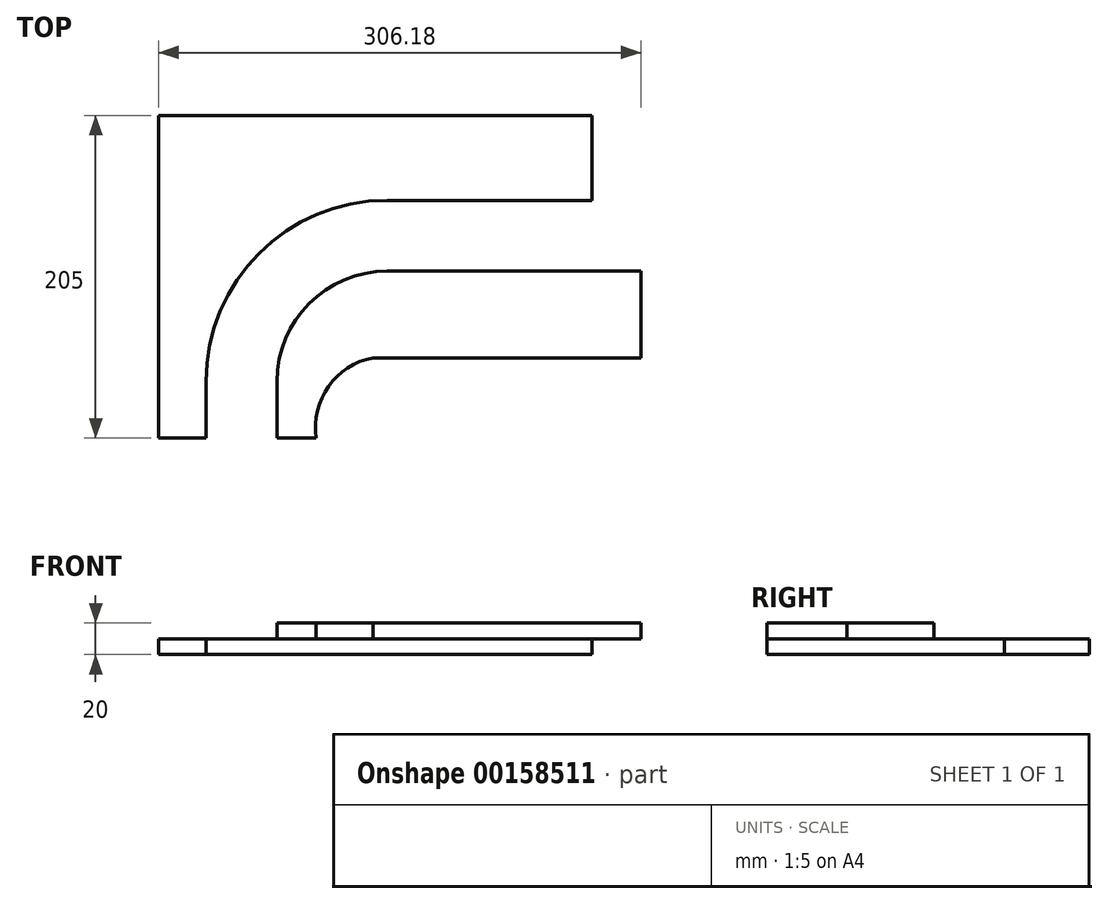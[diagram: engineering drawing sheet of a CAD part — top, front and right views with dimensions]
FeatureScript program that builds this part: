
annotation { "Feature Type Name" : "Feature", "Feature Type Description" : "" }
export const myFeature = defineFeature(function(context is Context, id is Id, definition is map)
    precondition{}
    {
        {
            var Q0;
            Q0=qCreatedBy(makeId("Top.planeOp"),FACE);
            var sketch = newSketch(context, id + "F0", { "sketchPlane" : qUnion([Q0])});
            skLineSegment(sketch, "E0.bottom", {"start": v(-230.67, 230.58) * mm, "end": v(44.33, 230.58) * mm});
            skLineSegment(sketch, "E0.top", {"start": v(-230.67, 25.58) * mm, "end": v(44.33, 25.58) * mm});
            skLineSegment(sketch, "E0.left", {"start": v(-230.67, 230.58) * mm, "end": v(-230.67, 25.58) * mm});
            skLineSegment(sketch, "E0.right", {"start": v(44.33, 230.58) * mm, "end": v(44.33, 25.58) * mm});
            skLineSegment(sketch, "E1.bottom", {"start": v(-209.28, -76.49) * mm, "end": v(30.72, -76.49) * mm});
            skLineSegment(sketch, "E1.top", {"start": v(-209.28, -196.49) * mm, "end": v(30.72, -196.49) * mm});
            skLineSegment(sketch, "E1.left", {"start": v(-209.28, -76.49) * mm, "end": v(-209.28, -196.49) * mm});
            skLineSegment(sketch, "E1.right", {"start": v(30.72, -76.49) * mm, "end": v(30.72, -196.49) * mm});
            skLineSegment(sketch, "E2", {"start": v(44.33, 230.58) * mm, "end": v(44.33, 176.58) * mm, "construction": true});
            skLineSegment(sketch, "E3", {"start": v(-230.67, 25.58) * mm, "end": v(-200.67, 25.58) * mm, "construction": true});
            skLineSegment(sketch, "E4", {"start": v(44.33, 176.58) * mm, "end": v(-85.67, 176.58) * mm, "construction": true});
            skLineSegment(sketch, "E5", {"start": v(-200.67, 25.58) * mm, "end": v(-200.67, 61.58) * mm, "construction": true});
            skLineSegment(sketch, "E6", {"start": v(-85.67, 176.58) * mm, "end": v(-85.67, 61.58) * mm, "construction": true});
            skLineSegment(sketch, "E7", {"start": v(-85.67, 61.58) * mm, "end": v(-200.67, 61.58) * mm, "construction": true});
            skCircle(sketch, "E8", {"center": v(-85.67, 61.58) * mm, "radius": 115 * mm});
            skLineSegment(sketch, "E9", {"start": v(-85.67, 176.58) * mm, "end": v(44.33, 176.58) * mm});
            skLineSegment(sketch, "E10", {"start": v(-200.67, 61.58) * mm, "end": v(-200.67, 25.58) * mm});
            skLineSegment(sketch, "E11", {"start": v(30.72, -76.49) * mm, "end": v(-94.48, -76.49) * mm, "construction": true});
            skLineSegment(sketch, "E12", {"start": v(-94.48, -76.49) * mm, "end": v(-94.48, -191.49) * mm, "construction": true});
            skCircle(sketch, "E13", {"center": v(-94.48, -191.49) * mm, "radius": 115 * mm});
            skLineSegment(sketch, "E14", {"start": v(30.72, -76.49) * mm, "end": v(30.72, -131.49) * mm, "construction": true});
            skLineSegment(sketch, "E15", {"start": v(30.72, -131.49) * mm, "end": v(-94.48, -131.49) * mm});
            skLineSegment(sketch, "E16", {"start": v(-209.28, -196.49) * mm, "end": v(-184.28, -196.49) * mm});
            skArc(sketch, "E17", {"start": v(-94.48, -131.49) * mm, "mid": v(-149.9, -149.44) * mm, "end": v(-184.28, -196.49) * mm});
            skLineSegment(sketch, "E18", {"start": v(-209.28, -196.49) * mm, "end": v(-209.28, -216.49) * mm});
            skLineSegment(sketch, "E19", {"start": v(-209.28, -216.49) * mm, "end": v(-184.28, -216.49) * mm});
            skLineSegment(sketch, "E20", {"start": v(-184.28, -216.49) * mm, "end": v(-184.28, -196.49) * mm});
            skSolve(sketch);
        }
        {
            var Q0;
            {var subQ1=sQuery(id+"F0.wireOp",EDGE,"E0.bottom");Q0=makeQuery(id+"F0.imprint","IMPRINT",FACE,{"disambiguationData":[TD([[makeQuery(id+"F0.imprint","IMPRINT",EDGE,{"derivedFrom":subQ1}),-1.0]])]});}
            extrude(context, id + "F1", {"entities" : qUnion([Q0]), "depth" : 10 * mm, "offsetDistance" : 25 * mm});
        }
        {
            var Q0;
            Q0=makeQuery(id+"F1.opExtrude","CAP_FACE",FACE,{"disambiguationData":[OSD([sQuery(id+"F0.wireOp",EDGE,"E0.bottom"),sQuery(id+"F0.wireOp",EDGE,"E0.top"),sQuery(id+"F0.wireOp",EDGE,"E0.left"),sQuery(id+"F0.wireOp",EDGE,"E0.right"),sQuery(id+"F0.wireOp",EDGE,"E8"),sQuery(id+"F0.wireOp",EDGE,"E9"),sQuery(id+"F0.wireOp",EDGE,"E10")])],"isStart":false});
            var sketch = newSketch(context, id + "F2", { "sketchPlane" : qUnion([Q0])});
            skLineSegment(sketch, "E21.0", {"start": v(-85.67, 176.58) * mm, "end": v(44.33, 176.58) * mm});
            skArc(sketch, "E21.1", {"start": v(-85.67, 176.58) * mm, "mid": v(-167, 142.9) * mm, "end": v(-200.67, 61.58) * mm});
            skLineSegment(sketch, "E21.2", {"start": v(-200.67, 61.58) * mm, "end": v(-200.67, 25.58) * mm});
            skLineSegment(sketch, "E22.0", {"start": v(-85.67, 131.58) * mm, "end": v(45.51, 131.58) * mm});
            skArc(sketch, "E22.1", {"start": v(-85.67, 131.58) * mm, "mid": v(-135.17, 111.07) * mm, "end": v(-155.67, 61.58) * mm});
            skLineSegment(sketch, "E22.2", {"start": v(-155.67, 61.58) * mm, "end": v(-155.67, 25.58) * mm});
            skLineSegment(sketch, "E23", {"start": v(45.51, 131.58) * mm, "end": v(45.51, 76.58) * mm});
            skLineSegment(sketch, "E24", {"start": v(45.51, 76.58) * mm, "end": v(-94.49, 76.58) * mm});
            skLineSegment(sketch, "E25", {"start": v(-155.67, 25.58) * mm, "end": v(-130.67, 25.58) * mm});
            skArc(sketch, "E26", {"start": v(-94.49, 76.58) * mm, "mid": v(-122.85, 58.37) * mm, "end": v(-130.67, 25.58) * mm});
            skLineSegment(sketch, "E27", {"start": v(45.51, 131.58) * mm, "end": v(75.51, 131.58) * mm});
            skLineSegment(sketch, "E28", {"start": v(75.51, 131.58) * mm, "end": v(75.51, 76.58) * mm});
            skLineSegment(sketch, "E29", {"start": v(75.51, 76.58) * mm, "end": v(45.51, 76.58) * mm});
            skSolve(sketch);
        }
        {
            var Q0;
            Q0=makeQuery(id+"F2.imprint","IMPRINT",FACE,{"disambiguationData":[TD([[makeQuery(id+"F2.imprint","IMPRINT",EDGE,{"derivedFrom":sQuery(id+"F2.wireOp",EDGE,"E23")}),1.0]])]});
            var Q1;
            Q1=makeQuery(id+"F2.imprint","IMPRINT",FACE,{"disambiguationData":[TD([[makeQuery(id+"F2.imprint","IMPRINT",EDGE,{"derivedFrom":sQuery(id+"F2.wireOp",EDGE,"E22.0")}),-1.0]])]});
            extrude(context, id + "F3", {"entities" : qUnion([Q0, Q1]), "depth" : 10 * mm, "offsetDistance" : 25 * mm});
        }
    });
